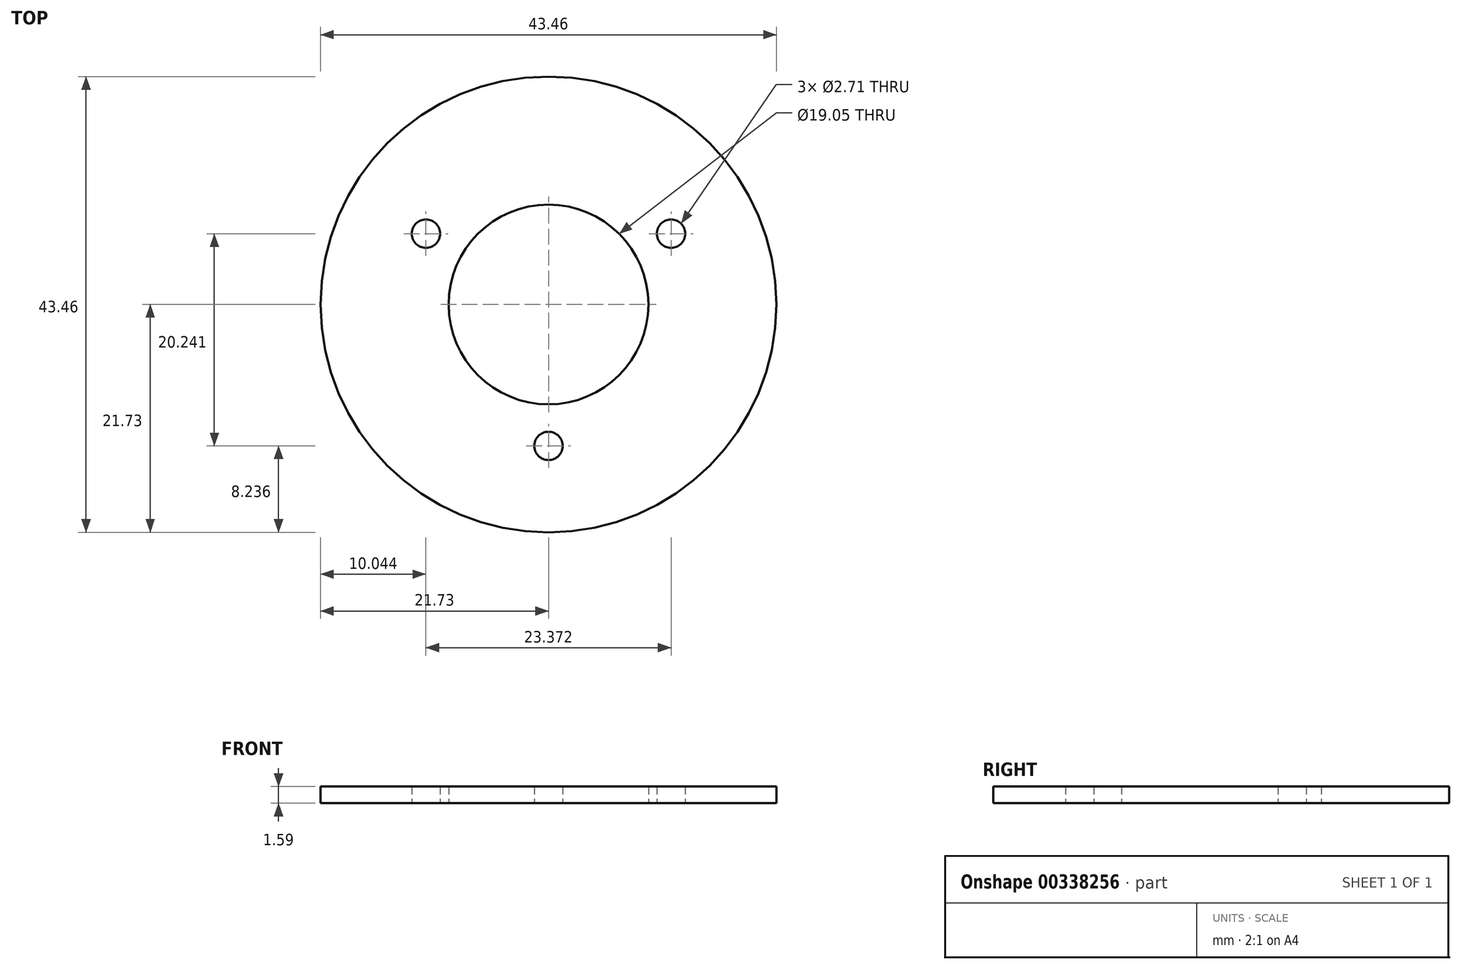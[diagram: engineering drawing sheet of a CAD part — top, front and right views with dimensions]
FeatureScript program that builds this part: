
annotation { "Feature Type Name" : "Feature", "Feature Type Description" : "" }
export const myFeature = defineFeature(function(context is Context, id is Id, definition is map)
    precondition{}
    {
        {
            var Q0;
            Q0=qCreatedBy(makeId("Top.planeOp"),FACE);
            var sketch = newSketch(context, id + "F0", { "sketchPlane" : qUnion([Q0])});
            skCircle(sketch, "E0", {"center": v(0, 0) * mm, "radius": 9.52 * mm});
            skCircle(sketch, "E1", {"center": v(0, 0) * mm, "radius": 21.73 * mm});
            skLineSegment(sketch, "E2", {"start": v(0, 0) * mm, "end": v(0, -13.5) * mm, "construction": true});
            skLineSegment(sketch, "E3", {"start": v(0, -13.5) * mm, "end": v(11.69, 6.75) * mm, "construction": true});
            skLineSegment(sketch, "E4", {"start": v(11.69, 6.75) * mm, "end": v(0, 0) * mm, "construction": true});
            skLineSegment(sketch, "E5", {"start": v(0, 0) * mm, "end": v(-11.69, 6.75) * mm, "construction": true});
            skLineSegment(sketch, "E6", {"start": v(-11.69, 6.75) * mm, "end": v(0, -13.5) * mm, "construction": true});
            skLineSegment(sketch, "E7", {"start": v(-11.69, 6.75) * mm, "end": v(11.69, 6.75) * mm, "construction": true});
            skCircle(sketch, "E8", {"center": v(0, -13.5) * mm, "radius": 3.97 * mm, "construction": true});
            skCircle(sketch, "E9", {"center": v(-11.69, 6.75) * mm, "radius": 1.35 * mm});
            skCircle(sketch, "E10", {"center": v(11.69, 6.75) * mm, "radius": 1.35 * mm});
            skCircle(sketch, "E11", {"center": v(0, -13.5) * mm, "radius": 1.35 * mm});
            skSolve(sketch);
        }
        {
            var Q0;
            Q0 = qSketchRegion(id + "F0", true);
            extrude(context, id + "F1", {"entities" : qUnion([Q0]), "depth" : 1.59 * mm});
        }
    });
